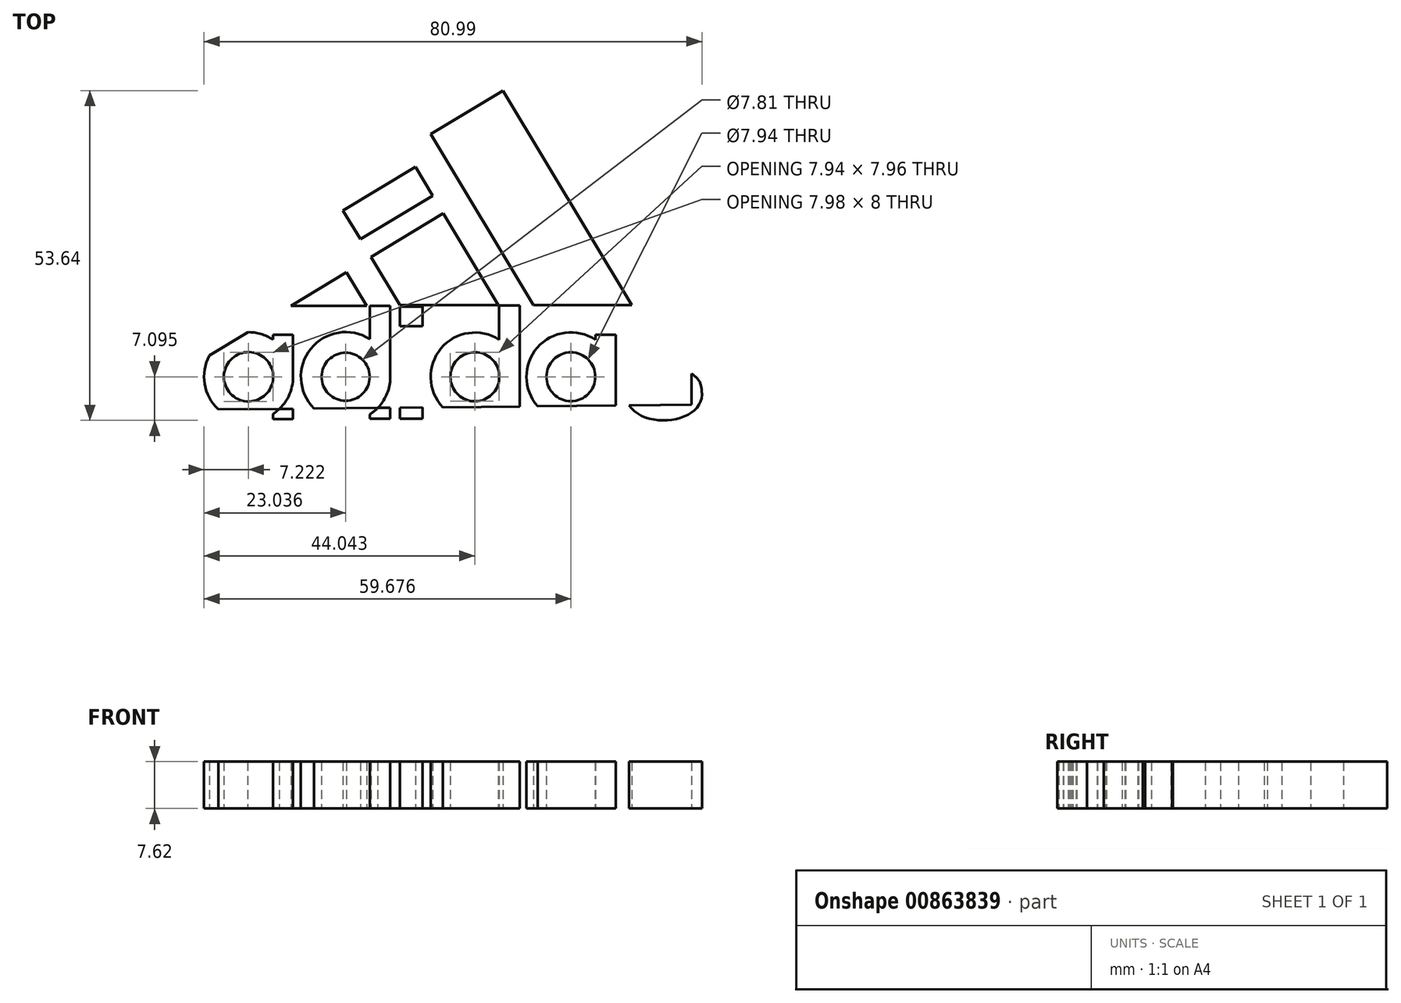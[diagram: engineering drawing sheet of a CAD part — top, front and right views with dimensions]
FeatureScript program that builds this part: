
annotation { "Feature Type Name" : "Feature", "Feature Type Description" : "" }
export const myFeature = defineFeature(function(context is Context, id is Id, definition is map)
    precondition{}
    {
        {
            var Q0;
            Q0=qCreatedBy(makeId("Top.planeOp"),FACE);
            var sketch = newSketch(context, id + "F0", { "sketchPlane" : qUnion([Q0])});
            skLineSegment(sketch, "E0", {"start": v(-60.8, 28.96) * mm, "end": v(-54.61, 18.8) * mm});
            skLineSegment(sketch, "E1", {"start": v(-54.61, 18.8) * mm, "end": v(-70.9, 18.8) * mm});
            skLineSegment(sketch, "E2", {"start": v(-70.9, 18.8) * mm, "end": v(-72.72, 21.86) * mm});
            skLineSegment(sketch, "E3", {"start": v(-72.72, 21.86) * mm, "end": v(-60.8, 28.96) * mm});
            skLineSegment(sketch, "E4", {"start": v(-46.68, 41.4) * mm, "end": v(-58.46, 34.32) * mm});
            skLineSegment(sketch, "E5", {"start": v(-58.46, 34.32) * mm, "end": v(-49.22, 18.94) * mm});
            skLineSegment(sketch, "E6", {"start": v(-49.22, 18.94) * mm, "end": v(-33.2, 18.94) * mm});
            skLineSegment(sketch, "E7", {"start": v(-33.2, 18.94) * mm, "end": v(-46.68, 41.4) * mm});
            skLineSegment(sketch, "E8", {"start": v(-44.2, 46.75) * mm, "end": v(-27.5, 18.94) * mm});
            skLineSegment(sketch, "E9", {"start": v(-27.5, 18.94) * mm, "end": v(-11.5, 18.94) * mm});
            skLineSegment(sketch, "E10", {"start": v(-11.5, 18.94) * mm, "end": v(-32.43, 53.81) * mm});
            skLineSegment(sketch, "E11", {"start": v(-32.43, 53.81) * mm, "end": v(-44.2, 46.75) * mm});
            skCircle(sketch, "E12", {"center": v(-73.83, 7.27) * mm, "radius": 4.01 * mm});
            skCircle(sketch, "E13", {"center": v(-73.83, 7.27) * mm, "radius": 7.25 * mm});
            skLineSegment(sketch, "E14.bottom", {"start": v(-69.87, 14.1) * mm, "end": v(-66.64, 14.1) * mm});
            skLineSegment(sketch, "E14.top", {"start": v(-69.87, 0.4) * mm, "end": v(-66.64, 0.4) * mm});
            skLineSegment(sketch, "E14.left", {"start": v(-69.87, 14.1) * mm, "end": v(-69.87, 0.4) * mm});
            skLineSegment(sketch, "E14.right", {"start": v(-66.64, 14.1) * mm, "end": v(-66.64, 0.4) * mm});
            skCircle(sketch, "E15", {"center": v(-58.04, 7.27) * mm, "radius": 3.9 * mm});
            skCircle(sketch, "E16", {"center": v(-58.04, 7.27) * mm, "radius": 7.27 * mm});
            skLineSegment(sketch, "E17.bottom", {"start": v(-54.11, 18.8) * mm, "end": v(-50.8, 18.8) * mm});
            skLineSegment(sketch, "E17.top", {"start": v(-54.11, 0.46) * mm, "end": v(-50.8, 0.46) * mm});
            skLineSegment(sketch, "E17.left", {"start": v(-54.11, 18.8) * mm, "end": v(-54.11, 0.46) * mm});
            skLineSegment(sketch, "E17.right", {"start": v(-50.8, 18.8) * mm, "end": v(-50.8, 0.46) * mm});
            skLineSegment(sketch, "E18.bottom", {"start": v(-49.22, 18.67) * mm, "end": v(-45.54, 18.67) * mm});
            skLineSegment(sketch, "E18.top", {"start": v(-49.22, 15.5) * mm, "end": v(-45.54, 15.5) * mm});
            skLineSegment(sketch, "E18.left", {"start": v(-49.22, 18.67) * mm, "end": v(-49.22, 15.5) * mm});
            skLineSegment(sketch, "E18.right", {"start": v(-45.54, 18.67) * mm, "end": v(-45.54, 15.5) * mm});
            skLineSegment(sketch, "E19.bottom", {"start": v(-49.22, 0.43) * mm, "end": v(-45.54, 0.43) * mm});
            skLineSegment(sketch, "E19.top", {"start": v(-49.22, 14.46) * mm, "end": v(-45.54, 14.46) * mm});
            skLineSegment(sketch, "E19.left", {"start": v(-49.22, 0.43) * mm, "end": v(-49.22, 14.46) * mm});
            skLineSegment(sketch, "E19.right", {"start": v(-45.54, 0.43) * mm, "end": v(-45.54, 14.46) * mm});
            skCircle(sketch, "E20", {"center": v(-37.01, 7.27) * mm, "radius": 4 * mm});
            skCircle(sketch, "E21", {"center": v(-37.01, 7.27) * mm, "radius": 7.2 * mm});
            skLineSegment(sketch, "E22.bottom", {"start": v(-33.07, 18.87) * mm, "end": v(-29.7, 18.87) * mm});
            skLineSegment(sketch, "E22.top", {"start": v(-33.07, 0.35) * mm, "end": v(-29.7, 0.35) * mm});
            skLineSegment(sketch, "E22.left", {"start": v(-33.07, 18.87) * mm, "end": v(-33.07, 0.35) * mm});
            skLineSegment(sketch, "E22.right", {"start": v(-29.7, 18.87) * mm, "end": v(-29.7, 0.35) * mm});
            skFitSpline(sketch, "E23", {"points": [v(-12.63, 4.95) * mm, v(-0.16, 4.99) * mm], "startDerivative": vector(0.74, -21.1) * mm, "endDerivative": vector(-3.31, 17.2) * mm});
            skFitSpline(sketch, "E24", {"points": [v(-0.16, 4.99) * mm, v(-8.61, 10.64) * mm], "startDerivative": vector(0.47, 14.03) * mm, "endDerivative": vector(1.41, 6.15) * mm});
            skFitSpline(sketch, "E25", {"points": [v(-8.61, 10.64) * mm, v(-4.03, 10.12) * mm], "startDerivative": vector(-0.65, 5.6) * mm, "endDerivative": vector(-1.2, -6.8) * mm});
            skLineSegment(sketch, "E26", {"start": v(-4.03, 10.12) * mm, "end": v(-0.49, 10.12) * mm});
            skFitSpline(sketch, "E27", {"points": [v(-0.49, 10.12) * mm, v(-12.14, 10.12) * mm], "startDerivative": vector(2.29, 15.82) * mm, "endDerivative": vector(-1.25, -20.43) * mm});
            skFitSpline(sketch, "E28", {"points": [v(-12.14, 10.12) * mm, v(-3.7, 4.45) * mm], "startDerivative": vector(-0.29, -14.9) * mm, "endDerivative": vector(0, -6.14) * mm});
            skFitSpline(sketch, "E29", {"points": [v(-3.7, 4.45) * mm, v(-8.97, 4.95) * mm], "startDerivative": vector(1.34, -5.18) * mm, "endDerivative": vector(-0.38, 8.74) * mm});
            skLineSegment(sketch, "E30", {"start": v(-12.63, 4.95) * mm, "end": v(-8.97, 4.95) * mm});
            skCircle(sketch, "E31", {"center": v(-21.4, 7.27) * mm, "radius": 3.97 * mm});
            skCircle(sketch, "E32", {"center": v(-21.4, 7.27) * mm, "radius": 7.22 * mm});
            skLineSegment(sketch, "E33.bottom", {"start": v(-17.42, 14.1) * mm, "end": v(-14.09, 14.1) * mm});
            skLineSegment(sketch, "E33.top", {"start": v(-17.42, 0.44) * mm, "end": v(-14.09, 0.44) * mm});
            skLineSegment(sketch, "E33.left", {"start": v(-17.42, 14.1) * mm, "end": v(-17.42, 0.44) * mm});
            skLineSegment(sketch, "E33.right", {"start": v(-14.09, 14.1) * mm, "end": v(-14.09, 0.44) * mm});
            skLineSegment(sketch, "E34", {"start": v(-83.97, -0.01) * mm, "end": v(-83.97, 12.66) * mm});
            skLineSegment(sketch, "E35", {"start": v(-83.97, 12.66) * mm, "end": v(-18.56, 51.92) * mm});
            skLineSegment(sketch, "E36", {"start": v(-18.56, 51.92) * mm, "end": v(0, 51.92) * mm});
            skLineSegment(sketch, "E37", {"start": v(0, 51.92) * mm, "end": v(0, 0) * mm});
            skLineSegment(sketch, "E38", {"start": v(0, 0) * mm, "end": v(-83.97, -0.01) * mm});
            skLineSegment(sketch, "E39", {"start": v(-83.97, 12.66) * mm, "end": v(-82.12, 9.57) * mm});
            skLineSegment(sketch, "E40", {"start": v(-82.12, 9.57) * mm, "end": v(-82.12, 1.9) * mm});
            skLineSegment(sketch, "E41", {"start": v(-82.12, 1.9) * mm, "end": v(-1.8, 2.72) * mm});
            skLineSegment(sketch, "E42", {"start": v(-1.8, 2.72) * mm, "end": v(-1.8, 49.05) * mm});
            skLineSegment(sketch, "E43", {"start": v(-1.8, 49.05) * mm, "end": v(-17.15, 49.05) * mm});
            skLineSegment(sketch, "E44", {"start": v(-17.15, 49.05) * mm, "end": v(-82.12, 9.57) * mm});
            skSolve(sketch);
        }
        {
            var Q0;
            {var subQ0=sQuery(id+"F0.wireOp",EDGE,"E33.left");var subQ1=sQuery(id+"F0.wireOp",EDGE,"E32");var subQ2=makeQuery(id+"F0.imprint","INTERSECT",VERTEX,{"disambiguationData":[OD(0.0)],"derivedFrom":[subQ1,subQ0]});Q0=makeQuery(id+"F0.imprint","IMPRINT",FACE,{"disambiguationData":[TD([[makeQuery(id+"F0.imprint","IMPRINT",EDGE,{"disambiguationData":[TD([[subQ2,1.0]])],"derivedFrom":subQ1}),1.0]])]});}
            var Q1;
            Q1=makeQuery(id+"F0.imprint","IMPRINT",FACE,{"disambiguationData":[TD([[makeQuery(id+"F0.imprint","IMPRINT",EDGE,{"derivedFrom":sQuery(id+"F0.wireOp",EDGE,"E8")}),1.0]])]});
            var Q2;
            Q2=makeQuery(id+"F0.imprint","IMPRINT",FACE,{"disambiguationData":[TD([[makeQuery(id+"F0.imprint","IMPRINT",EDGE,{"derivedFrom":sQuery(id+"F0.wireOp",EDGE,"E0")}),-1.0]])]});
            var Q3;
            {var subQ5=sQuery(id+"F0.wireOp",EDGE,"E17.top");Q3=makeQuery(id+"F0.imprint","IMPRINT",FACE,{"disambiguationData":[TD([[makeQuery(id+"F0.imprint","IMPRINT",EDGE,{"derivedFrom":subQ5}),1.0]])]});}
            var Q4;
            {var subQ0=sQuery(id+"F0.wireOp",EDGE,"E14.left");var subQ1=sQuery(id+"F0.wireOp",EDGE,"E12");var subQ2=makeQuery(id+"F0.imprint","INTERSECT",VERTEX,{"disambiguationData":[OD(0.0)],"derivedFrom":[subQ1,subQ0]});Q4=makeQuery(id+"F0.imprint","IMPRINT",FACE,{"disambiguationData":[TD([[makeQuery(id+"F0.imprint","IMPRINT",EDGE,{"disambiguationData":[TD([[subQ2,-1.0]])],"derivedFrom":subQ1}),-1.0]])]});}
            var Q5;
            {var subQ0=sQuery(id+"F0.wireOp",EDGE,"E22.left");var subQ1=sQuery(id+"F0.wireOp",EDGE,"E20");var subQ2=makeQuery(id+"F0.imprint","INTERSECT",VERTEX,{"disambiguationData":[OD(0.0)],"derivedFrom":[subQ1,subQ0]});Q5=makeQuery(id+"F0.imprint","IMPRINT",FACE,{"disambiguationData":[TD([[makeQuery(id+"F0.imprint","IMPRINT",EDGE,{"disambiguationData":[TD([[subQ2,1.0]])],"derivedFrom":subQ1}),-1.0]])]});}
            var Q6;
            {var subQ5=sQuery(id+"F0.wireOp",EDGE,"E14.bottom");Q6=makeQuery(id+"F0.imprint","IMPRINT",FACE,{"disambiguationData":[TD([[makeQuery(id+"F0.imprint","IMPRINT",EDGE,{"derivedFrom":subQ5}),-1.0]])]});}
            var Q7;
            {var subQ1=sQuery(id+"F0.wireOp",EDGE,"E22.bottom");Q7=makeQuery(id+"F0.imprint","IMPRINT",FACE,{"disambiguationData":[TD([[makeQuery(id+"F0.imprint","IMPRINT",EDGE,{"derivedFrom":subQ1}),-1.0]])]});}
            var Q8;
            Q8=makeQuery(id+"F0.imprint","IMPRINT",FACE,{"disambiguationData":[TD([[makeQuery(id+"F0.imprint","IMPRINT",EDGE,{"derivedFrom":sQuery(id+"F0.wireOp",EDGE,"E4")}),1.0]])]});
            var Q9;
            Q9=makeQuery(id+"F0.imprint","IMPRINT",FACE,{"disambiguationData":[TD([[makeQuery(id+"F0.imprint","IMPRINT",EDGE,{"derivedFrom":sQuery(id+"F0.wireOp",EDGE,"E15")}),-1.0]])]});
            var Q10;
            Q10=makeQuery(id+"F0.imprint","IMPRINT",FACE,{"disambiguationData":[TD([[makeQuery(id+"F0.imprint","IMPRINT",EDGE,{"derivedFrom":sQuery(id+"F0.wireOp",EDGE,"E19.bottom")}),1.0]])]});
            var Q11;
            {var subQ0=sQuery(id+"F0.wireOp",EDGE,"E14.left");var subQ1=sQuery(id+"F0.wireOp",EDGE,"E12");var subQ2=makeQuery(id+"F0.imprint","INTERSECT",VERTEX,{"disambiguationData":[OD(0.0)],"derivedFrom":[subQ1,subQ0]});Q11=makeQuery(id+"F0.imprint","IMPRINT",FACE,{"disambiguationData":[TD([[makeQuery(id+"F0.imprint","IMPRINT",EDGE,{"disambiguationData":[TD([[subQ2,1.0]])],"derivedFrom":subQ1}),-1.0]])]});}
            var Q12;
            {var subQ5=sQuery(id+"F0.wireOp",EDGE,"E17.bottom");Q12=makeQuery(id+"F0.imprint","IMPRINT",FACE,{"disambiguationData":[TD([[makeQuery(id+"F0.imprint","IMPRINT",EDGE,{"derivedFrom":subQ5}),-1.0]])]});}
            var Q13;
            Q13=makeQuery(id+"F0.imprint","IMPRINT",FACE,{"disambiguationData":[TD([[makeQuery(id+"F0.imprint","IMPRINT",EDGE,{"derivedFrom":sQuery(id+"F0.wireOp",EDGE,"E23")}),1.0]])]});
            var Q14;
            Q14=makeQuery(id+"F0.imprint","IMPRINT",FACE,{"disambiguationData":[TD([[makeQuery(id+"F0.imprint","IMPRINT",EDGE,{"derivedFrom":sQuery(id+"F0.wireOp",EDGE,"E18.bottom")}),-1.0]])]});
            var Q15;
            {var subQ0=sQuery(id+"F0.wireOp",EDGE,"E22.left");var subQ1=sQuery(id+"F0.wireOp",EDGE,"E20");var subQ2=makeQuery(id+"F0.imprint","INTERSECT",VERTEX,{"disambiguationData":[OD(0.0)],"derivedFrom":[subQ1,subQ0]});Q15=makeQuery(id+"F0.imprint","IMPRINT",FACE,{"disambiguationData":[TD([[makeQuery(id+"F0.imprint","IMPRINT",EDGE,{"disambiguationData":[TD([[subQ2,-1.0]])],"derivedFrom":subQ1}),-1.0]])]});}
            var Q16;
            {var subQ1=sQuery(id+"F0.wireOp",EDGE,"E33.bottom");Q16=makeQuery(id+"F0.imprint","IMPRINT",FACE,{"disambiguationData":[TD([[makeQuery(id+"F0.imprint","IMPRINT",EDGE,{"derivedFrom":subQ1}),-1.0]])]});}
            var Q17;
            {var subQ5=sQuery(id+"F0.wireOp",EDGE,"E14.top");Q17=makeQuery(id+"F0.imprint","IMPRINT",FACE,{"disambiguationData":[TD([[makeQuery(id+"F0.imprint","IMPRINT",EDGE,{"derivedFrom":subQ5}),1.0]])]});}
            var Q18;
            {var subQ0=sQuery(id+"F0.wireOp",EDGE,"E17.left");var subQ1=sQuery(id+"F0.wireOp",EDGE,"E16");var subQ2=makeQuery(id+"F0.imprint","INTERSECT",VERTEX,{"disambiguationData":[OD(0.0)],"derivedFrom":[subQ1,subQ0]});Q18=makeQuery(id+"F0.imprint","IMPRINT",FACE,{"disambiguationData":[TD([[makeQuery(id+"F0.imprint","IMPRINT",EDGE,{"disambiguationData":[TD([[subQ2,1.0]])],"derivedFrom":subQ1}),1.0]])]});}
            var Q19;
            Q19=makeQuery(id+"F0.imprint","IMPRINT",FACE,{"disambiguationData":[TD([[makeQuery(id+"F0.imprint","IMPRINT",EDGE,{"derivedFrom":sQuery(id+"F0.wireOp",EDGE,"E31")}),-1.0]])]});
            var Q20;
            {var subQ0=sQuery(id+"F0.wireOp",EDGE,"E17.right");var subQ1=sQuery(id+"F0.wireOp",EDGE,"E16");var subQ2=makeQuery(id+"F0.imprint","INTERSECT",VERTEX,{"disambiguationData":[OD(0.0)],"derivedFrom":[subQ1,subQ0]});Q20=makeQuery(id+"F0.imprint","IMPRINT",FACE,{"disambiguationData":[TD([[makeQuery(id+"F0.imprint","IMPRINT",EDGE,{"disambiguationData":[TD([[subQ2,1.0]])],"derivedFrom":subQ1}),1.0]])]});}
            var Q21;
            {var subQ0=sQuery(id+"F0.wireOp",EDGE,"E14.left");var subQ1=sQuery(id+"F0.wireOp",EDGE,"E12");var subQ2=makeQuery(id+"F0.imprint","INTERSECT",VERTEX,{"disambiguationData":[OD(0.0)],"derivedFrom":[subQ1,subQ0]});Q21=makeQuery(id+"F0.imprint","IMPRINT",FACE,{"disambiguationData":[TD([[makeQuery(id+"F0.imprint","IMPRINT",EDGE,{"disambiguationData":[TD([[subQ2,1.0]])],"derivedFrom":subQ1}),1.0]])]});}
            var Q22;
            {var subQ0=sQuery(id+"F0.wireOp",EDGE,"E22.left");var subQ1=sQuery(id+"F0.wireOp",EDGE,"E20");var subQ2=makeQuery(id+"F0.imprint","INTERSECT",VERTEX,{"disambiguationData":[OD(0.0)],"derivedFrom":[subQ1,subQ0]});Q22=makeQuery(id+"F0.imprint","IMPRINT",FACE,{"disambiguationData":[TD([[makeQuery(id+"F0.imprint","IMPRINT",EDGE,{"disambiguationData":[TD([[subQ2,1.0]])],"derivedFrom":subQ1}),1.0]])]});}
            var Q23;
            {var subQ0=sQuery(id+"F0.wireOp",EDGE,"E14.right");var subQ1=sQuery(id+"F0.wireOp",EDGE,"E13");var subQ2=makeQuery(id+"F0.imprint","INTERSECT",VERTEX,{"disambiguationData":[OD(0.0)],"derivedFrom":[subQ1,subQ0]});Q23=makeQuery(id+"F0.imprint","IMPRINT",FACE,{"disambiguationData":[TD([[makeQuery(id+"F0.imprint","IMPRINT",EDGE,{"disambiguationData":[TD([[subQ2,1.0]])],"derivedFrom":subQ1}),1.0]])]});}
            var Q24;
            {var subQ0=sQuery(id+"F0.wireOp",EDGE,"E6");Q24=makeQuery(id+"F0.imprint","IMPRINT",FACE,{"disambiguationData":[TD([[makeQuery(id+"F0.imprint","IMPRINT",EDGE,{"derivedFrom":subQ0}),1.0]])]});}
            extrude(context, id + "F1", {"entities" : qUnion([Q0, Q1, Q2, Q3, Q4, Q5, Q6, Q7, Q8, Q9, Q10, Q11, Q12, Q13, Q14, Q15, Q16, Q17, Q18, Q19, Q20, Q21, Q22, Q23, Q24]), "depth" : 7.62 * mm, "offsetDistance" : 25.4 * mm});
        }
    });
